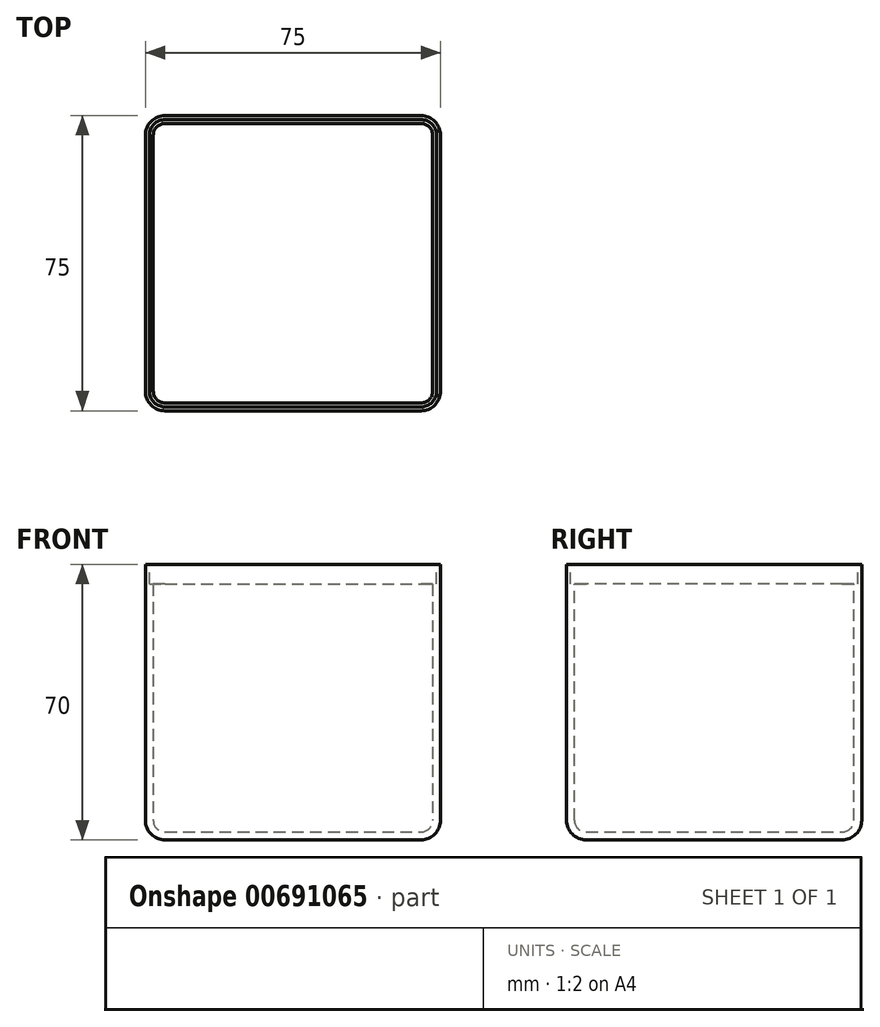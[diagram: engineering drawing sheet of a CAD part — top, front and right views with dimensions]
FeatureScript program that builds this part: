
annotation { "Feature Type Name" : "Feature", "Feature Type Description" : "" }
export const myFeature = defineFeature(function(context is Context, id is Id, definition is map)
    precondition{}
    {
        {
            var Q0;
            Q0=qCreatedBy(makeId("Top.planeOp"),FACE);
            var sketch = newSketch(context, id + "F0", { "sketchPlane" : qUnion([Q0])});
            skLineSegment(sketch, "E0.bottom", {"start": v(-37.5, 37.5) * mm, "end": v(37.5, 37.5) * mm});
            skLineSegment(sketch, "E0.top", {"start": v(-37.5, -37.5) * mm, "end": v(37.5, -37.5) * mm});
            skLineSegment(sketch, "E0.left", {"start": v(-37.5, 37.5) * mm, "end": v(-37.5, -37.5) * mm});
            skLineSegment(sketch, "E0.right", {"start": v(37.5, 37.5) * mm, "end": v(37.5, -37.5) * mm});
            skPoint(sketch, "E0.middle", {"position": v(0, 0) * mm});
            skLineSegment(sketch, "E1.0", {"start": v(-35.5, 35.5) * mm, "end": v(35.5, 35.5) * mm});
            skLineSegment(sketch, "E1.1", {"start": v(-35.5, 35.5) * mm, "end": v(-35.5, -35.5) * mm});
            skLineSegment(sketch, "E1.2", {"start": v(-35.5, -35.5) * mm, "end": v(35.5, -35.5) * mm});
            skLineSegment(sketch, "E1.3", {"start": v(35.5, 35.5) * mm, "end": v(35.5, -35.5) * mm});
            skSolve(sketch);
        }
        {
            var Q0;
            Q0=makeQuery(id+"F0.imprint","IMPRINT",FACE,{"disambiguationData":[TD([[makeQuery(id+"F0.imprint","IMPRINT",EDGE,{"derivedFrom":sQuery(id+"F0.wireOp",EDGE,"E1.0")}),-1.0]])]});
            var Q1;
            Q1=makeQuery(id+"F0.imprint","IMPRINT",FACE,{"disambiguationData":[TD([[makeQuery(id+"F0.imprint","IMPRINT",EDGE,{"derivedFrom":sQuery(id+"F0.wireOp",EDGE,"E0.bottom")}),-1.0]])]});
            extrude(context, id + "F1", {"entities" : qUnion([Q0, Q1]), "depth" : 70 * mm, "offsetDistance" : 25 * mm});
        }
        {
            var Q0;
            Q0=makeQuery(id+"F1.opExtrude","SWEPT_EDGE",EDGE,{"disambiguationData":[OSD([sQuery(id+"F0.wireOp",EDGE,"E0.top"),sQuery(id+"F0.wireOp",EDGE,"E0.left")])]});
            var Q1;
            Q1=makeQuery(id+"F1.opExtrude","SWEPT_EDGE",EDGE,{"disambiguationData":[OSD([sQuery(id+"F0.wireOp",EDGE,"E0.top"),sQuery(id+"F0.wireOp",EDGE,"E0.right")])]});
            var Q2;
            Q2=makeQuery(id+"F1.opExtrude","CAP_EDGE",EDGE,{"disambiguationData":[OSD([sQuery(id+"F0.wireOp",EDGE,"E0.top")])],"isStart":true});
            var Q3;
            Q3=makeQuery(id+"F1.opExtrude","CAP_EDGE",EDGE,{"disambiguationData":[OSD([sQuery(id+"F0.wireOp",EDGE,"E0.left")])],"isStart":true});
            var Q4;
            Q4=makeQuery(id+"F1.opExtrude","SWEPT_EDGE",EDGE,{"disambiguationData":[OSD([sQuery(id+"F0.wireOp",EDGE,"E0.bottom"),sQuery(id+"F0.wireOp",EDGE,"E0.left")])]});
            var Q5;
            Q5=makeQuery(id+"F1.opExtrude","CAP_EDGE",EDGE,{"disambiguationData":[OSD([sQuery(id+"F0.wireOp",EDGE,"E0.bottom")])],"isStart":true});
            var Q6;
            Q6=makeQuery(id+"F1.opExtrude","SWEPT_EDGE",EDGE,{"disambiguationData":[OSD([sQuery(id+"F0.wireOp",EDGE,"E0.bottom"),sQuery(id+"F0.wireOp",EDGE,"E0.right")])]});
            var Q7;
            Q7=makeQuery(id+"F1.opExtrude","CAP_EDGE",EDGE,{"disambiguationData":[OSD([sQuery(id+"F0.wireOp",EDGE,"E0.right")])],"isStart":true});
            fillet(context, id + "F2", {"entities" : qUnion([Q0, Q1, Q2, Q3, Q4, Q5, Q6, Q7]), "radius" : 5 * mm, "tangentPropagation" : true, "allowEdgeOverflow" : false});
        }
        {
            var Q0;
            Q0=makeQuery(id+"F1.opExtrude","CAP_FACE",FACE,{"disambiguationData":[OSD([sQuery(id+"F0.wireOp",EDGE,"E0.bottom"),sQuery(id+"F0.wireOp",EDGE,"E0.top"),sQuery(id+"F0.wireOp",EDGE,"E0.left"),sQuery(id+"F0.wireOp",EDGE,"E0.right")])],"isStart":false});
            shell(context, id + "F3", {"entities" : qUnion([Q0]), "thickness" : 2 * mm});
        }
        {
            var Q0;
            Q0=makeQuery(id+"F1.opExtrude","CAP_FACE",FACE,{"disambiguationData":[OSD([sQuery(id+"F0.wireOp",EDGE,"E0.bottom"),sQuery(id+"F0.wireOp",EDGE,"E0.top"),sQuery(id+"F0.wireOp",EDGE,"E0.left"),sQuery(id+"F0.wireOp",EDGE,"E0.right")])],"isStart":false});
            cPlane(context, id + "F4", {"entities" : qUnion([Q0]), "cplaneType" : CPlaneType.OFFSET, "offset" : 0 * mm, "width" : 150 * mm, "height" : 150 * mm});
        }
        {
            var Q0;
            Q0=qCreatedBy(id+"F4.planeOp",FACE);
            var sketch = newSketch(context, id + "F5", { "sketchPlane" : qUnion([Q0])});
            skArc(sketch, "E2.0", {"start": v(-36.5, -32.5) * mm, "mid": v(-35.33, -35.33) * mm, "end": v(-32.5, -36.5) * mm});
            skLineSegment(sketch, "E2.1", {"start": v(-36.5, 32.5) * mm, "end": v(-36.5, -32.5) * mm});
            skLineSegment(sketch, "E2.2", {"start": v(-32.5, -36.5) * mm, "end": v(32.5, -36.5) * mm});
            skArc(sketch, "E2.3", {"start": v(-32.5, 36.5) * mm, "mid": v(-35.33, 35.33) * mm, "end": v(-36.5, 32.5) * mm});
            skArc(sketch, "E2.4", {"start": v(32.5, -36.5) * mm, "mid": v(35.33, -35.33) * mm, "end": v(36.5, -32.5) * mm});
            skLineSegment(sketch, "E2.5", {"start": v(36.5, 32.5) * mm, "end": v(36.5, -32.5) * mm});
            skArc(sketch, "E2.6", {"start": v(36.5, 32.5) * mm, "mid": v(35.33, 35.33) * mm, "end": v(32.5, 36.5) * mm});
            skLineSegment(sketch, "E2.7", {"start": v(-32.5, 36.5) * mm, "end": v(32.5, 36.5) * mm});
            skSolve(sketch);
        }
        {
            var Q0;
            Q0=makeQuery(id+"F5.imprint","IMPRINT",FACE,{"disambiguationData":[TD([[makeQuery(id+"F5.imprint","IMPRINT",EDGE,{"derivedFrom":sQuery(id+"F5.wireOp",EDGE,"E2.0")}),1.0]])]});
            extrude(context, id + "F6", {"entities" : qUnion([Q0]), "operationType" : NewBodyOperationType.REMOVE, "oppositeDirection" : true, "depth" : 5 * mm, "offsetDistance" : 25 * mm});
        }
    });
